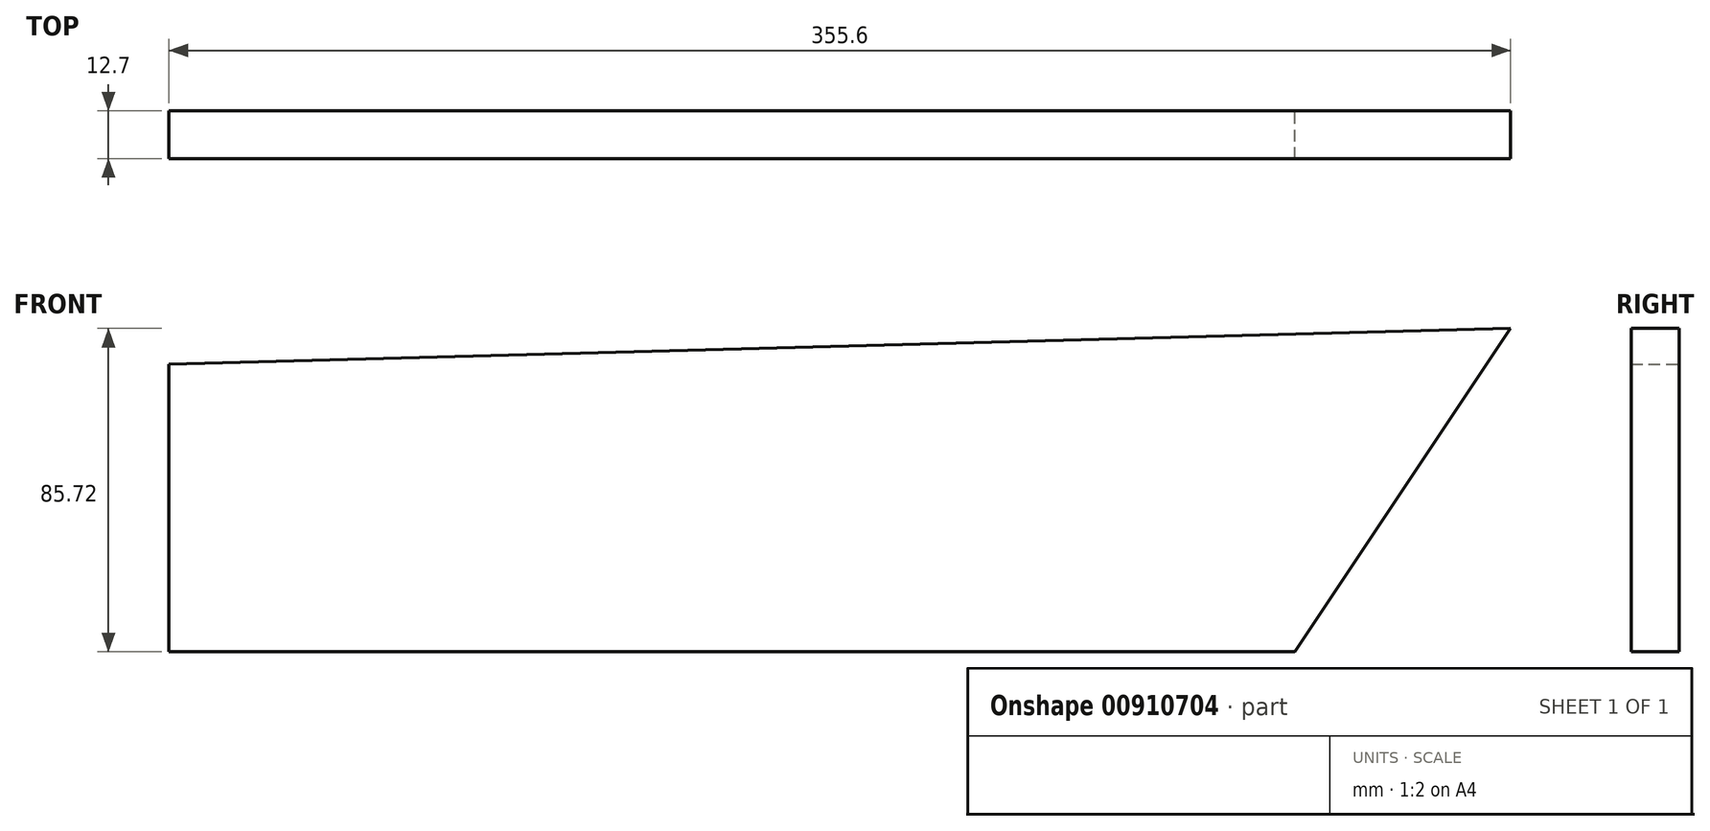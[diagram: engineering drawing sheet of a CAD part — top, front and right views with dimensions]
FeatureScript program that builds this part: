
annotation { "Feature Type Name" : "Feature", "Feature Type Description" : "" }
export const myFeature = defineFeature(function(context is Context, id is Id, definition is map)
    precondition{}
    {
        {
            var Q0;
            Q0=qCreatedBy(makeId("Front.planeOp"),FACE);
            var sketch = newSketch(context, id + "F0", { "sketchPlane" : qUnion([Q0])});
            skLineSegment(sketch, "E0", {"start": v(0, 0) * mm, "end": v(0, -76.2) * mm});
            skLineSegment(sketch, "E1", {"start": v(0, -76.2) * mm, "end": v(298.45, -76.2) * mm});
            skLineSegment(sketch, "E2", {"start": v(298.45, -76.2) * mm, "end": v(355.6, 9.52) * mm});
            skLineSegment(sketch, "E3", {"start": v(355.6, 9.52) * mm, "end": v(0, 0) * mm});
            skSolve(sketch);
        }
        {
            var Q0;
            Q0=makeQuery(id+"F0.imprint","IMPRINT",FACE,{"disambiguationData":[TD([[makeQuery(id+"F0.imprint","IMPRINT",EDGE,{"derivedFrom":sQuery(id+"F0.wireOp",EDGE,"E0")}),1.0]])]});
            extrude(context, id + "F1", {"entities" : qUnion([Q0]), "depth" : 12.7 * mm, "offsetDistance" : 25.4 * mm});
        }
    });
